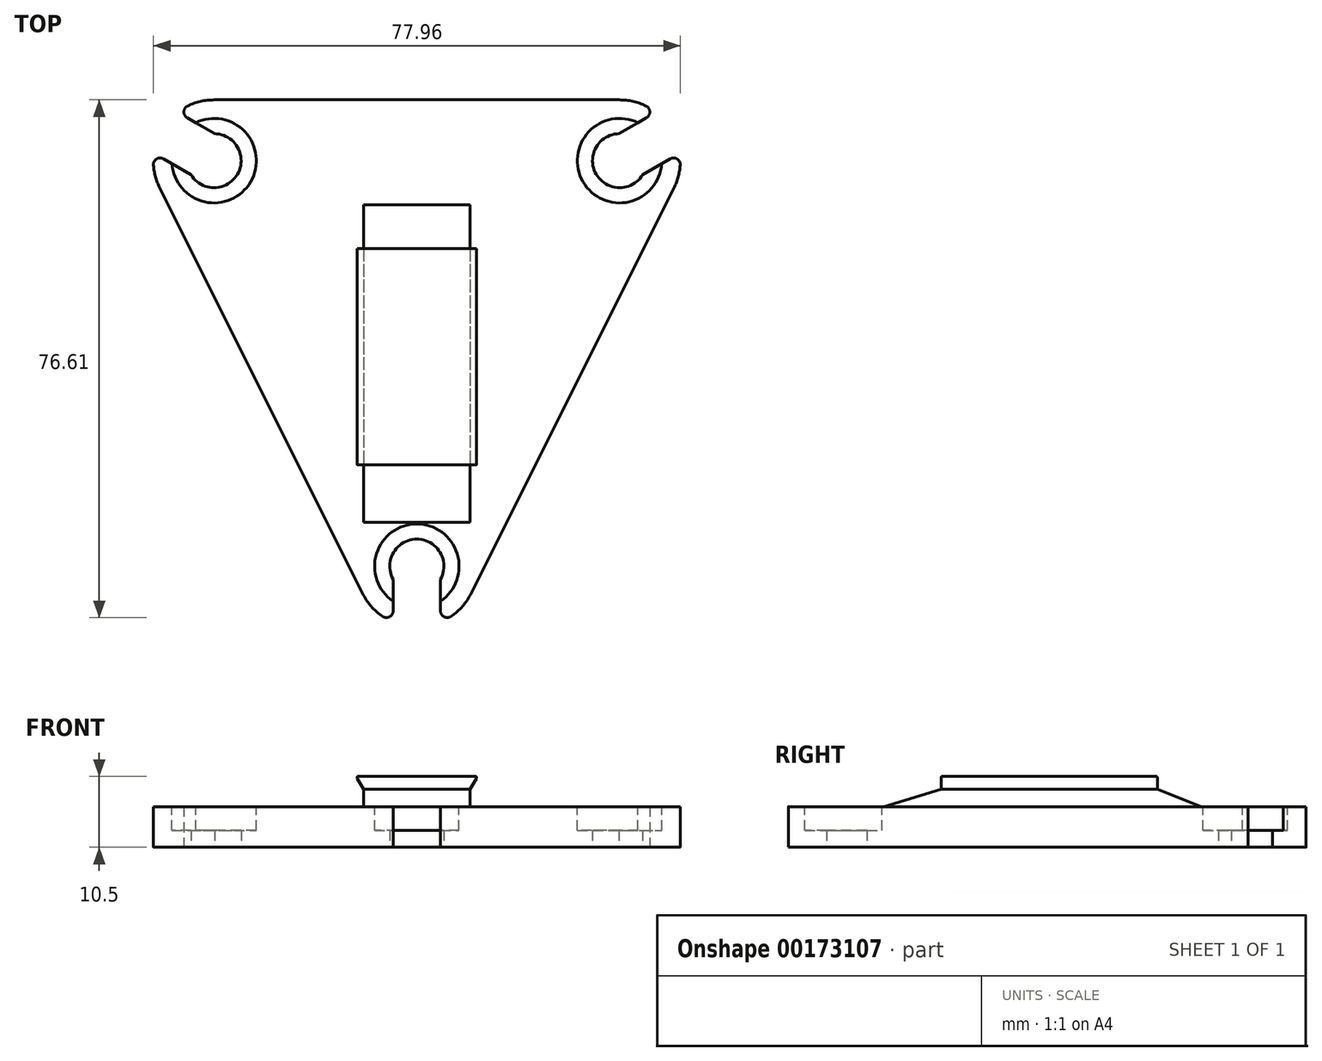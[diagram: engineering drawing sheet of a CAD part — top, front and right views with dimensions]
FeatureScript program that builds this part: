
annotation { "Feature Type Name" : "Feature", "Feature Type Description" : "" }
export const myFeature = defineFeature(function(context is Context, id is Id, definition is map)
    precondition{}
    {
        {
            var Q0;
            Q0=qCreatedBy(makeId("Top.planeOp"),FACE);
            var sketch = newSketch(context, id + "F0", { "sketchPlane" : qUnion([Q0])});
            skArc(sketch, "E0", {"start": v(-33.43, 57.94) * mm, "mid": v(-26.54, 58) * mm, "end": v(-29.93, 64) * mm});
            skArc(sketch, "E1", {"start": v(3.5, -1.94) * mm, "mid": v(0, 4) * mm, "end": v(-3.5, -1.94) * mm});
            skLineSegment(sketch, "E2", {"start": v(0, 0) * mm, "end": v(0, 213.32) * mm, "construction": true});
            skArc(sketch, "E3.MirrorC", {"start": v(33.43, 57.94) * mm, "mid": v(26.54, 58) * mm, "end": v(29.93, 64) * mm});
            skArc(sketch, "E4.0", {"start": v(-30, 69) * mm, "mid": v(-32, 68.77) * mm, "end": v(-33.91, 68.1) * mm});
            skArc(sketch, "E5.0", {"start": v(30, 69) * mm, "mid": v(32, 68.77) * mm, "end": v(33.91, 68.1) * mm});
            skArc(sketch, "E6.0", {"start": v(-8.05, -4.02) * mm, "mid": v(-6.78, -5.92) * mm, "end": v(-5.06, -7.44) * mm});
            skLineSegment(sketch, "E7", {"start": v(38.05, 55.98) * mm, "end": v(8.05, -4.02) * mm});
            skLineSegment(sketch, "E8", {"start": v(-38.05, 55.98) * mm, "end": v(-8.05, -4.02) * mm});
            skLineSegment(sketch, "E9", {"start": v(-30, 69) * mm, "end": v(30, 69) * mm});
            skLineSegment(sketch, "E10", {"start": v(-29.93, 64) * mm, "end": v(-33.98, 66.34) * mm});
            skLineSegment(sketch, "E11", {"start": v(-33.43, 57.94) * mm, "end": v(-37.48, 60.28) * mm});
            skLineSegment(sketch, "E12", {"start": v(-30, 60) * mm, "end": v(-42.01, 66.93) * mm, "construction": true});
            skLineSegment(sketch, "E13", {"start": v(-30, 60) * mm, "end": v(30, 60) * mm, "construction": true});
            skArc(sketch, "E14.trimOffspring", {"start": v(-38.98, 59.34) * mm, "mid": v(-38.68, 57.61) * mm, "end": v(-38.05, 55.98) * mm});
            skArc(sketch, "E15", {"start": v(-37.48, 60.28) * mm, "mid": v(-38.5, 60.26) * mm, "end": v(-38.98, 59.34) * mm});
            skArc(sketch, "E16", {"start": v(-33.91, 68.1) * mm, "mid": v(-34.48, 67.24) * mm, "end": v(-33.98, 66.34) * mm});
            skArc(sketch, "E17.MirrorCS", {"start": v(33.91, 68.1) * mm, "mid": v(34.48, 67.24) * mm, "end": v(33.98, 66.34) * mm});
            skLineSegment(sketch, "E18.MirrorCS", {"start": v(29.93, 64) * mm, "end": v(33.98, 66.34) * mm});
            skLineSegment(sketch, "E19.MirrorCS", {"start": v(33.43, 57.94) * mm, "end": v(37.48, 60.28) * mm});
            skArc(sketch, "E20.MirrorCS", {"start": v(37.48, 60.28) * mm, "mid": v(38.5, 60.26) * mm, "end": v(38.98, 59.34) * mm});
            skArc(sketch, "E21.trimOffspring", {"start": v(38.98, 59.34) * mm, "mid": v(38.68, 57.61) * mm, "end": v(38.05, 55.98) * mm});
            skLineSegment(sketch, "E22", {"start": v(-3.5, -1.94) * mm, "end": v(-3.5, -6.61) * mm});
            skLineSegment(sketch, "E23", {"start": v(3.5, -1.94) * mm, "end": v(3.5, -6.61) * mm});
            skArc(sketch, "E24", {"start": v(-5.06, -7.44) * mm, "mid": v(-4.03, -7.5) * mm, "end": v(-3.5, -6.61) * mm});
            skArc(sketch, "E25.MirrorC", {"start": v(5.06, -7.44) * mm, "mid": v(4.03, -7.5) * mm, "end": v(3.5, -6.61) * mm});
            skArc(sketch, "E26.trimOffspring", {"start": v(5.06, -7.44) * mm, "mid": v(6.78, -5.92) * mm, "end": v(8.05, -4.02) * mm});
            skSolve(sketch);
        }
        {
            var Q0;
            Q0 = qSketchRegion(id + "F0", true);
            extrude(context, id + "F1", {"entities" : qUnion([Q0]), "depth" : 6 * mm});
        }
        {
            var Q0;
            Q0=makeQuery(id+"F1.opExtrude","CAP_FACE",FACE,{"disambiguationData":[OSD([sQuery(id+"F0.wireOp",EDGE,"E0"),sQuery(id+"F0.wireOp",EDGE,"E1"),sQuery(id+"F0.wireOp",EDGE,"E3.MirrorC"),sQuery(id+"F0.wireOp",EDGE,"E4.0"),sQuery(id+"F0.wireOp",EDGE,"E5.0"),sQuery(id+"F0.wireOp",EDGE,"E6.0"),sQuery(id+"F0.wireOp",EDGE,"E7"),sQuery(id+"F0.wireOp",EDGE,"E8"),sQuery(id+"F0.wireOp",EDGE,"E9"),sQuery(id+"F0.wireOp",EDGE,"E10"),sQuery(id+"F0.wireOp",EDGE,"E11"),sQuery(id+"F0.wireOp",EDGE,"E14.trimOffspring"),sQuery(id+"F0.wireOp",EDGE,"E15"),sQuery(id+"F0.wireOp",EDGE,"E16"),sQuery(id+"F0.wireOp",EDGE,"E17.MirrorCS"),sQuery(id+"F0.wireOp",EDGE,"E18.MirrorCS"),sQuery(id+"F0.wireOp",EDGE,"E19.MirrorCS"),sQuery(id+"F0.wireOp",EDGE,"E20.MirrorCS"),sQuery(id+"F0.wireOp",EDGE,"E21.trimOffspring"),sQuery(id+"F0.wireOp",EDGE,"E22"),sQuery(id+"F0.wireOp",EDGE,"E23"),sQuery(id+"F0.wireOp",EDGE,"E24"),sQuery(id+"F0.wireOp",EDGE,"E25.MirrorC"),sQuery(id+"F0.wireOp",EDGE,"E26.trimOffspring")])],"isStart":false});
            var sketch = newSketch(context, id + "F2", { "sketchPlane" : qUnion([Q0])});
            skCircle(sketch, "E27", {"center": v(-30, 60) * mm, "radius": 6.25 * mm});
            skCircle(sketch, "E28", {"center": v(0, 0) * mm, "radius": 6.25 * mm});
            skLineSegment(sketch, "E29", {"start": v(0, 0) * mm, "end": v(0, 32) * mm, "construction": true});
            skCircle(sketch, "E30.MirrorC", {"center": v(30, 60) * mm, "radius": 6.25 * mm});
            skSolve(sketch);
        }
        {
            var Q0;
            Q0 = qSketchRegion(id + "F2", true);
            extrude(context, id + "F3", {"entities" : qUnion([Q0]), "operationType" : NewBodyOperationType.REMOVE, "oppositeDirection" : true, "depth" : 3.5 * mm});
        }
        {
            var Q0;
            Q0=makeQuery(id+"F1.opExtrude","CAP_FACE",FACE,{"disambiguationData":[OSD([sQuery(id+"F0.wireOp",EDGE,"E0"),sQuery(id+"F0.wireOp",EDGE,"E1"),sQuery(id+"F0.wireOp",EDGE,"E3.MirrorC"),sQuery(id+"F0.wireOp",EDGE,"E4.0"),sQuery(id+"F0.wireOp",EDGE,"E5.0"),sQuery(id+"F0.wireOp",EDGE,"E6.0"),sQuery(id+"F0.wireOp",EDGE,"E7"),sQuery(id+"F0.wireOp",EDGE,"E8"),sQuery(id+"F0.wireOp",EDGE,"E9"),sQuery(id+"F0.wireOp",EDGE,"E10"),sQuery(id+"F0.wireOp",EDGE,"E11"),sQuery(id+"F0.wireOp",EDGE,"E14.trimOffspring"),sQuery(id+"F0.wireOp",EDGE,"E15"),sQuery(id+"F0.wireOp",EDGE,"E16"),sQuery(id+"F0.wireOp",EDGE,"E17.MirrorCS"),sQuery(id+"F0.wireOp",EDGE,"E18.MirrorCS"),sQuery(id+"F0.wireOp",EDGE,"E19.MirrorCS"),sQuery(id+"F0.wireOp",EDGE,"E20.MirrorCS"),sQuery(id+"F0.wireOp",EDGE,"E21.trimOffspring"),sQuery(id+"F0.wireOp",EDGE,"E22"),sQuery(id+"F0.wireOp",EDGE,"E23"),sQuery(id+"F0.wireOp",EDGE,"E24"),sQuery(id+"F0.wireOp",EDGE,"E25.MirrorC"),sQuery(id+"F0.wireOp",EDGE,"E26.trimOffspring")])],"isStart":false});
            var sketch = newSketch(context, id + "F4", { "sketchPlane" : qUnion([Q0])});
            skLineSegment(sketch, "E31.bottom", {"start": v(-7.9, 47) * mm, "end": v(7.9, 47) * mm});
            skLineSegment(sketch, "E31.top", {"start": v(-7.9, 15) * mm, "end": v(7.9, 15) * mm});
            skLineSegment(sketch, "E31.left", {"start": v(-7.9, 47) * mm, "end": v(-7.9, 15) * mm});
            skLineSegment(sketch, "E31.right", {"start": v(7.9, 47) * mm, "end": v(7.9, 15) * mm});
            skPoint(sketch, "E31.middle", {"position": v(0, 31) * mm});
            skSolve(sketch);
        }
        {
            var Q0;
            Q0 = qSketchRegion(id + "F4", true);
            extrude(context, id + "F5", {"entities" : qUnion([Q0]), "operationType" : NewBodyOperationType.ADD, "depth" : 4.5 * mm});
        }
        {
            var Q0;
            Q0=makeQuery(id+"F5.opExtrude","SWEPT_FACE",FACE,{"disambiguationData":[OSD([sQuery(id+"F4.wireOp",EDGE,"E31.top")])]});
            var sketch = newSketch(context, id + "F6", { "sketchPlane" : qUnion([Q0])});
            skLineSegment(sketch, "E32", {"start": v(7.9, 10.5) * mm, "end": v(9, 10.5) * mm});
            skLineSegment(sketch, "E33", {"start": v(9, 10.5) * mm, "end": v(7.9, 8.6) * mm});
            skLineSegment(sketch, "E34", {"start": v(7.9, 8.6) * mm, "end": v(7.9, 10.5) * mm});
            skLineSegment(sketch, "E35", {"start": v(0, 10.5) * mm, "end": v(0, 12.7) * mm, "construction": true});
            skPoint(sketch, "E35.endSnap0", {"position": v(0, 10.5) * mm});
            skLineSegment(sketch, "E36.MirrorCS", {"start": v(-7.9, 10.5) * mm, "end": v(-9, 10.5) * mm});
            skLineSegment(sketch, "E37.MirrorCS", {"start": v(-9, 10.5) * mm, "end": v(-7.9, 8.6) * mm});
            skLineSegment(sketch, "E38.MirrorCS", {"start": v(-7.9, 8.6) * mm, "end": v(-7.9, 10.5) * mm});
            skSolve(sketch);
        }
        {
            var Q0;
            Q0 = qSketchRegion(id + "F6", true);
            extrude(context, id + "F7", {"entities" : qUnion([Q0]), "operationType" : NewBodyOperationType.ADD, "oppositeDirection" : true, "depth" : 32 * mm});
        }
        {
            var Q0;
            Q0=makeQuery(id+"F5.opExtrude","SWEPT_FACE",FACE,{"disambiguationData":[OSD([sQuery(id+"F4.wireOp",EDGE,"E31.left")])]});
            var sketch = newSketch(context, id + "F8", { "sketchPlane" : qUnion([Q0])});
            skLineSegment(sketch, "E39", {"start": v(-15, 8.6) * mm, "end": v(-6.5, 6) * mm});
            skLineSegment(sketch, "E40", {"start": v(-6.5, 6) * mm, "end": v(-15, 6) * mm});
            skLineSegment(sketch, "E41", {"start": v(-15, 6) * mm, "end": v(-15, 8.6) * mm});
            skLineSegment(sketch, "E42", {"start": v(-47, 8.6) * mm, "end": v(-53.5, 6) * mm});
            skLineSegment(sketch, "E43", {"start": v(-53.5, 6) * mm, "end": v(-47, 6) * mm});
            skLineSegment(sketch, "E44", {"start": v(-47, 6) * mm, "end": v(-47, 8.6) * mm});
            skSolve(sketch);
        }
        {
            var Q0;
            Q0 = qSketchRegion(id + "F8", true);
            extrude(context, id + "F9", {"entities" : qUnion([Q0]), "operationType" : NewBodyOperationType.ADD, "oppositeDirection" : true, "depth" : 15.8 * mm});
        }
        {
            var Q0;
            Q0=makeQuery(id+"F7.opExtrude","SWEPT_EDGE",EDGE,{"disambiguationData":[OSD([sQuery(id+"F6.wireOp",EDGE,"E36.MirrorCS"),sQuery(id+"F6.wireOp",EDGE,"E37.MirrorCS")])]});
            var Q1;
            Q1=makeQuery(id+"F7.opExtrude","SWEPT_EDGE",EDGE,{"disambiguationData":[OSD([sQuery(id+"F6.wireOp",EDGE,"E32"),sQuery(id+"F6.wireOp",EDGE,"E33")])]});
            var Q2;
            Q2=makeQuery(id+"F7.boolean.opBoolean","MERGE",EDGE,{"derivedFrom":[makeQuery(id+"F5.opExtrude","CAP_EDGE",EDGE,{"disambiguationData":[OSD([sQuery(id+"F4.wireOp",EDGE,"E31.top")])],"isStart":false}),makeQuery(id+"F7.opExtrude","CAP_EDGE",EDGE,{"disambiguationData":[OSD([sQuery(id+"F6.wireOp",EDGE,"E32")])],"isStart":true}),makeQuery(id+"F7.opExtrude","CAP_EDGE",EDGE,{"disambiguationData":[OSD([sQuery(id+"F6.wireOp",EDGE,"E36.MirrorCS")])],"isStart":true})]});
            var Q3;
            Q3=makeQuery(id+"F7.boolean.opBoolean","MERGE",EDGE,{"derivedFrom":[makeQuery(id+"F5.opExtrude","CAP_EDGE",EDGE,{"disambiguationData":[OSD([sQuery(id+"F4.wireOp",EDGE,"E31.bottom")])],"isStart":false}),makeQuery(id+"F7.opExtrude","CAP_EDGE",EDGE,{"disambiguationData":[OSD([sQuery(id+"F6.wireOp",EDGE,"E32")])],"isStart":false}),makeQuery(id+"F7.opExtrude","CAP_EDGE",EDGE,{"disambiguationData":[OSD([sQuery(id+"F6.wireOp",EDGE,"E36.MirrorCS")])],"isStart":false})]});
            fillet(context, id + "F10", {"entities" : qUnion([Q0, Q1, Q2, Q3]), "radius" : .2 * mm, "tangentPropagation" : true, "allowEdgeOverflow" : false});
        }
    });
